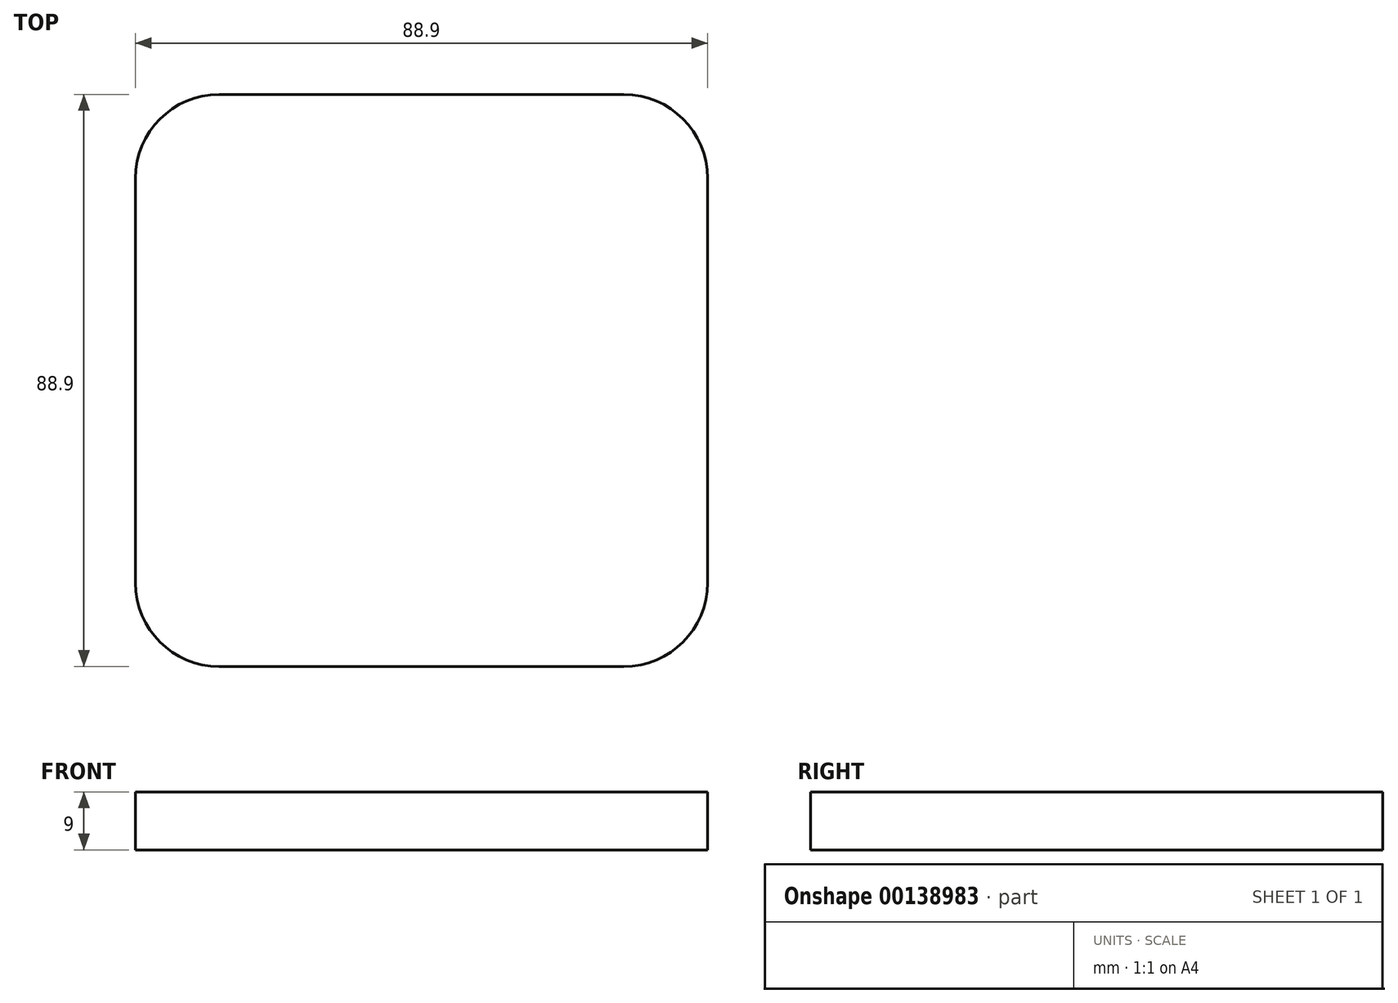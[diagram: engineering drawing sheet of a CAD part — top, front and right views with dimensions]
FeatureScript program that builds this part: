
annotation { "Feature Type Name" : "Feature", "Feature Type Description" : "" }
export const myFeature = defineFeature(function(context is Context, id is Id, definition is map)
    precondition{}
    {
        {
            var Q0;
            Q0=qCreatedBy(makeId("Top.planeOp"),FACE);
            var sketch = newSketch(context, id + "F0", { "sketchPlane" : qUnion([Q0])});
            skLineSegment(sketch, "E0.bottom", {"start": v(44.45, -44.45) * mm, "end": v(-44.45, -44.45) * mm});
            skLineSegment(sketch, "E0.top", {"start": v(44.45, 44.45) * mm, "end": v(-44.45, 44.45) * mm});
            skLineSegment(sketch, "E0.left", {"start": v(44.45, -44.45) * mm, "end": v(44.45, 44.45) * mm});
            skLineSegment(sketch, "E0.right", {"start": v(-44.45, -44.45) * mm, "end": v(-44.45, 44.45) * mm});
            skPoint(sketch, "E0.middle", {"position": v(0, 0) * mm});
            skSolve(sketch);
        }
        {
            var Q0;
            Q0=makeQuery(id+"F0.imprint","IMPRINT",FACE,{"disambiguationData":[TD([[makeQuery(id+"F0.imprint","IMPRINT",EDGE,{"derivedFrom":sQuery(id+"F0.wireOp",EDGE,"E0.bottom")}),-1.0]])]});
            extrude(context, id + "F1", {"entities" : qUnion([Q0]), "endBound" : BoundingType.SYMMETRIC, "depth" : 9 * mm});
        }
        {
            var Q0;
            Q0=makeQuery(id+"F1.opExtrude","SWEPT_EDGE",EDGE,{"disambiguationData":[OSD([sQuery(id+"F0.wireOp",EDGE,"E0.bottom"),sQuery(id+"F0.wireOp",EDGE,"E0.left")])]});
            var Q1;
            Q1=makeQuery(id+"F1.opExtrude","SWEPT_EDGE",EDGE,{"disambiguationData":[OSD([sQuery(id+"F0.wireOp",EDGE,"E0.top"),sQuery(id+"F0.wireOp",EDGE,"E0.left")])]});
            var Q2;
            Q2=makeQuery(id+"F1.opExtrude","SWEPT_EDGE",EDGE,{"disambiguationData":[OSD([sQuery(id+"F0.wireOp",EDGE,"E0.top"),sQuery(id+"F0.wireOp",EDGE,"E0.right")])]});
            var Q3;
            Q3=makeQuery(id+"F1.opExtrude","SWEPT_EDGE",EDGE,{"disambiguationData":[OSD([sQuery(id+"F0.wireOp",EDGE,"E0.bottom"),sQuery(id+"F0.wireOp",EDGE,"E0.right")])]});
            fillet(context, id + "F2", {"entities" : qUnion([Q0, Q1, Q2, Q3]), "radius" : 13 * mm, "tangentPropagation" : true, "allowEdgeOverflow" : false});
        }
    });
